# Revit family: Salzbehälter
name_source: partatom
category: HLS-Bauteile
units: mm (PartAtom-declared; Revit-internal decimal feet)

## family parameters
Arbeitsebenenbasiert = Nein
Beim Laden mit Abzugskörper schneiden = Nein
Bemaßung runder Anschluss = Durchmesser verwenden
Beschriftungsausrichtung beibehalten = Nein
Gemeinsam genutzt = Nein
Immer vertikal = Ja
Klassifizierung = Keine
Raumberechnungspunkt = Nein
Teiletyp = Normal

## types (11) — shared parameters
Homepage = https://www.burkhalter-h2o.ch
LUT = Salzbehälter
ZD = 75 mm
zero-valued in all types: Vorgabe-Ansicht

## per-type parameters (varying)
| type | D | D1 | E | E1 | HB | Typ |
| Salzbehälter - 15L | 480 mm  [stored 1.5748 ft] | 600 mm  [stored 1.9685 ft] | 785 mm | 725 mm  [stored 2.37861 ft] | 800 mm  [stored 2.62467 ft] | 15L |
| Salzbehälter - 25L | 480 mm  [stored 1.5748 ft] | 600 mm  [stored 1.9685 ft] | 785 mm | 725 mm  [stored 2.37861 ft] | 800 mm  [stored 2.62467 ft] | 25L |
| Salzbehälter - 50L | 570 mm  [stored 1.87008 ft] | 680 mm  [stored 2.23097 ft] | 830 mm  [stored 2.7231 ft] | 770 mm  [stored 2.52625 ft] | 845 mm  [stored 2.77231 ft] | 50L |
| Salzbehälter - 75L | 570 mm  [stored 1.87008 ft] | 680 mm  [stored 2.23097 ft] | 830 mm  [stored 2.7231 ft] | 770 mm  [stored 2.52625 ft] | 845 mm  [stored 2.77231 ft] | 75L |
| Salzbehälter - 100L | 660 mm  [stored 2.16535 ft] | 765 mm  [stored 2.50984 ft] | 1000 mm  [stored 3.28084 ft] | 940 mm  [stored 3.08399 ft] | 1015 mm  [stored 3.33005 ft] | 100L |
| Salzbehälter - 125L | 660 mm  [stored 2.16535 ft] | 765 mm  [stored 2.50984 ft] | 1000 mm  [stored 3.28084 ft] | 940 mm  [stored 3.08399 ft] | 1015 mm  [stored 3.33005 ft] | 125L |
| Salzbehälter - 150L | 760 mm | 875 mm  [stored 2.87073 ft] | 925 mm  [stored 3.03478 ft] | 865 mm  [stored 2.83793 ft] | 940 mm  [stored 3.08399 ft] | 150L |
| Salzbehälter - 200L | 760 mm | 875 mm  [stored 2.87073 ft] | 925 mm  [stored 3.03478 ft] | 865 mm  [stored 2.83793 ft] | 940 mm  [stored 3.08399 ft] | 200L |
| Salzbehälter - 250L | 760 mm | 875 mm  [stored 2.87073 ft] | 925 mm  [stored 3.03478 ft] | 865 mm  [stored 2.83793 ft] | 940 mm  [stored 3.08399 ft] | 250L |
| Salzbehälter - 300L | 890 mm  [stored 2.91995 ft] | 1000 mm  [stored 3.28084 ft] | 1090 mm  [stored 3.57612 ft] | 1030 mm  [stored 3.37927 ft] | 1105 mm  [stored 3.62533 ft] | 300L |
| Salzbehälter - 400L | 890 mm  [stored 2.91995 ft] | 1000 mm  [stored 3.28084 ft] | 1090 mm  [stored 3.57612 ft] | 1030 mm  [stored 3.37927 ft] | 1105 mm  [stored 3.62533 ft] | 400L |

note: [stored X ft] marks values corroborated as IEEE doubles in the binary element streams (Revit-internal decimal feet)
